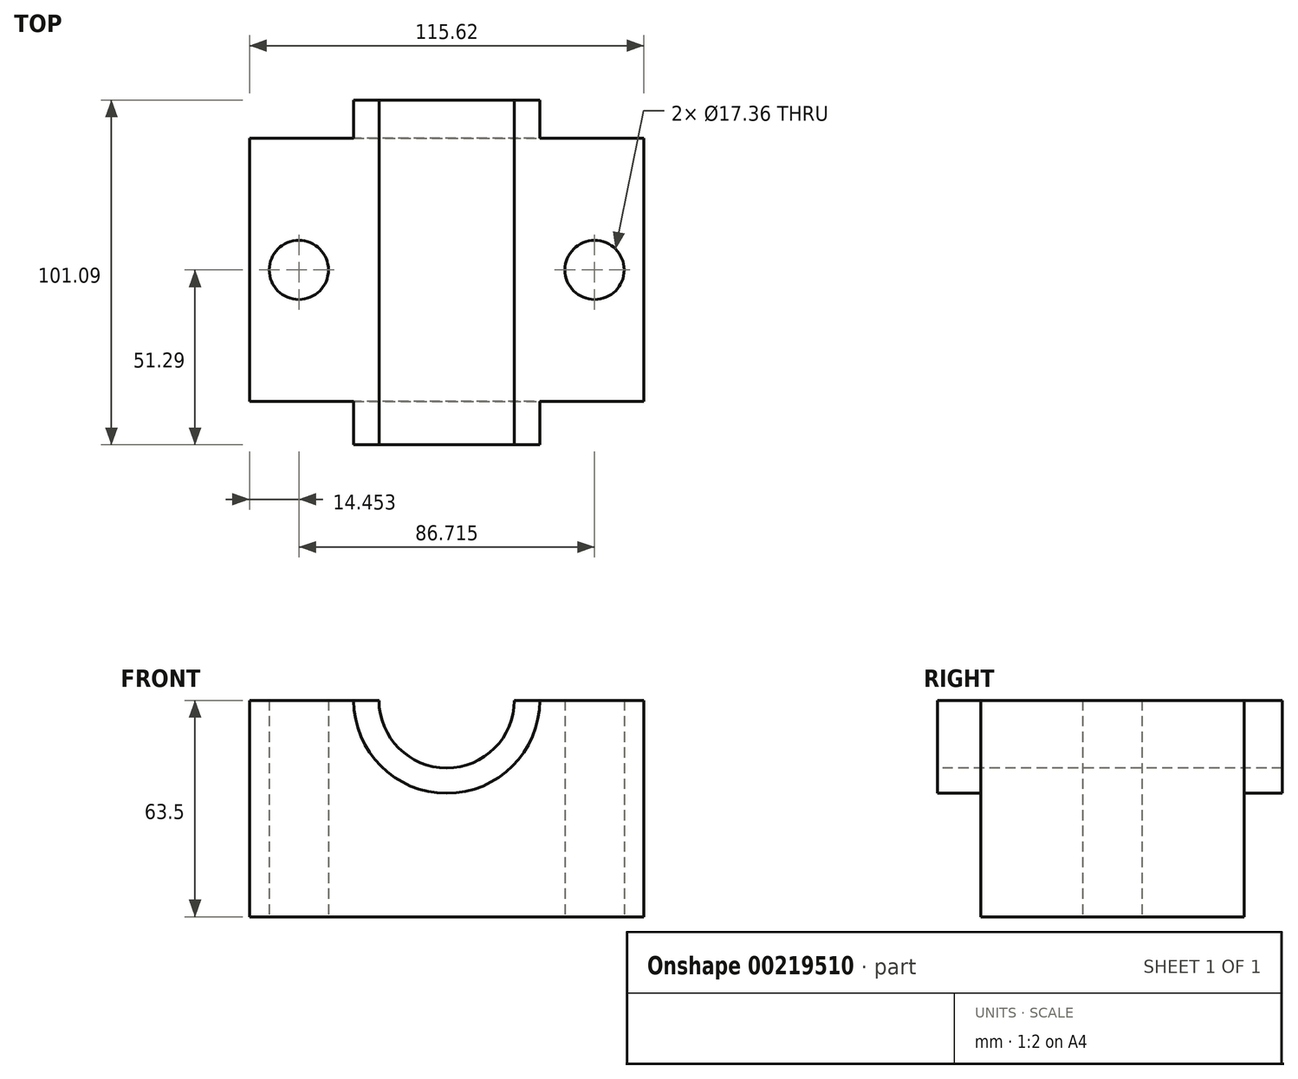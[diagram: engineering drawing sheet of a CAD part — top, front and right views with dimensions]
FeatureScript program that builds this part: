
annotation { "Feature Type Name" : "Feature", "Feature Type Description" : "" }
export const myFeature = defineFeature(function(context is Context, id is Id, definition is map)
    precondition{}
    {
        {
            var Q0;
            Q0=qCreatedBy(makeId("Top.planeOp"),FACE);
            var sketch = newSketch(context, id + "F0", { "sketchPlane" : qUnion([Q0])});
            skLineSegment(sketch, "E0.bottom", {"start": v(57.8, 38.59) * mm, "end": v(-57.8, 38.59) * mm});
            skLineSegment(sketch, "E0.top", {"start": v(57.8, -38.59) * mm, "end": v(-57.8, -38.59) * mm});
            skLineSegment(sketch, "E0.left", {"start": v(57.8, 38.59) * mm, "end": v(57.8, -38.59) * mm});
            skLineSegment(sketch, "E0.right", {"start": v(-57.8, 38.59) * mm, "end": v(-57.8, -38.59) * mm});
            skPoint(sketch, "E0.middle", {"position": v(0, 0) * mm});
            skCircle(sketch, "E1", {"center": v(43.36, 0) * mm, "radius": 8.68 * mm});
            skCircle(sketch, "E2.MirrorC", {"center": v(-43.36, 0) * mm, "radius": 8.68 * mm});
            skSolve(sketch);
        }
        {
            var Q0;
            Q0 = qSketchRegion(id + "F0", true);
            extrude(context, id + "F1", {"entities" : qUnion([Q0]), "depth" : 63.5 * mm});
        }
        {
            var Q0;
            Q0=makeQuery(id+"F1.opExtrude","SWEPT_FACE",FACE,{"disambiguationData":[OSD([sQuery(id+"F0.wireOp",EDGE,"E0.top")])]});
            var sketch = newSketch(context, id + "F2", { "sketchPlane" : qUnion([Q0])});
            skCircle(sketch, "E3", {"center": v(0, 63.5) * mm, "radius": 27.28 * mm});
            skSolve(sketch);
        }
        {
            var Q0;
            Q0 = qSketchRegion(id + "F2", true);
            extrude(context, id + "F3", {"entities" : qUnion([Q0]), "operationType" : NewBodyOperationType.ADD, "depth" : 12.7 * mm});
        }
        {
            var Q0;
            Q0=makeQuery(id+"F3.opExtrude","CAP_FACE",FACE,{"disambiguationData":[OSD([sQuery(id+"F2.wireOp",EDGE,"E3")])],"isStart":false});
            var sketch = newSketch(context, id + "F4", { "sketchPlane" : qUnion([Q0])});
            skCircle(sketch, "E4", {"center": v(0, 63.5) * mm, "radius": 27.28 * mm});
            skCircle(sketch, "E5", {"center": v(0, 63.5) * mm, "radius": 19.85 * mm});
            skSolve(sketch);
        }
        {
            var Q0;
            Q0 = qSketchRegion(id + "F4", true);
            extrude(context, id + "F5", {"entities" : qUnion([Q0]), "operationType" : NewBodyOperationType.ADD, "oppositeDirection" : true, "depth" : 101.1 * mm});
        }
        {
            var Q0;
            Q0=makeQuery(id+"F5.opExtrude","CAP_FACE",FACE,{"disambiguationData":[OSD([sQuery(id+"F4.wireOp",EDGE,"E4"),sQuery(id+"F4.wireOp",EDGE,"E5")])],"isStart":false});
            var sketch = newSketch(context, id + "F6", { "sketchPlane" : qUnion([Q0])});
            skLineSegment(sketch, "E6.bottom", {"start": v(27.28, 63.5) * mm, "end": v(19.85, 63.5) * mm});
            skLineSegment(sketch, "E6.top", {"start": v(27.28, 94.86) * mm, "end": v(-27.28, 94.86) * mm});
            skLineSegment(sketch, "E6.left", {"start": v(27.28, 63.5) * mm, "end": v(27.28, 94.86) * mm});
            skLineSegment(sketch, "E6.right", {"start": v(-27.28, 63.5) * mm, "end": v(-27.28, 94.86) * mm});
            skArc(sketch, "E7", {"start": v(-19.85, 63.5) * mm, "mid": v(0, 43.65) * mm, "end": v(19.85, 63.5) * mm});
            skLineSegment(sketch, "E8.trimOffspring", {"start": v(-19.85, 63.5) * mm, "end": v(-27.28, 63.5) * mm});
            skSolve(sketch);
        }
        {
            var Q0;
            Q0 = qSketchRegion(id + "F6", true);
            extrude(context, id + "F7", {"entities" : qUnion([Q0]), "operationType" : NewBodyOperationType.REMOVE, "oppositeDirection" : true, "depth" : 194.82 * mm});
        }
    });
